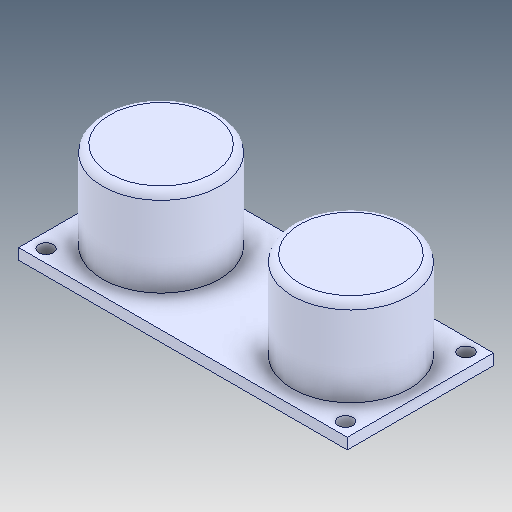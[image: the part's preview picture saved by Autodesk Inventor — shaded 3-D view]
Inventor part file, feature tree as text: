
AUTODESK INVENTOR PART (.ipt)
format: ipt  version: 2020 (Build 240168000, 168)  size: 160,256 bytes
history: mixed  units: mm
features: fillet x1, imported_body x1
ambient origin geometry x8: Origin, YZ Plane, XZ Plane, XY Plane, X Axis, Y Axis, Z Axis, Center Point
bodies: Solid1 (imported_parasolid)
feature tree (2):
  fillet  "Fillet1"  [1 undecoded]
  imported_body  NMx_Import_Brep_tag  [imported B-rep: ~16 faces, bbox_mm=[45.0, 13.5, 20.0]]
note: 1 required parameter value undecoded (feature->parameter linkage not recoverable at this tier; creation-order binding heuristic only, values carry confidence <= 0.55)
